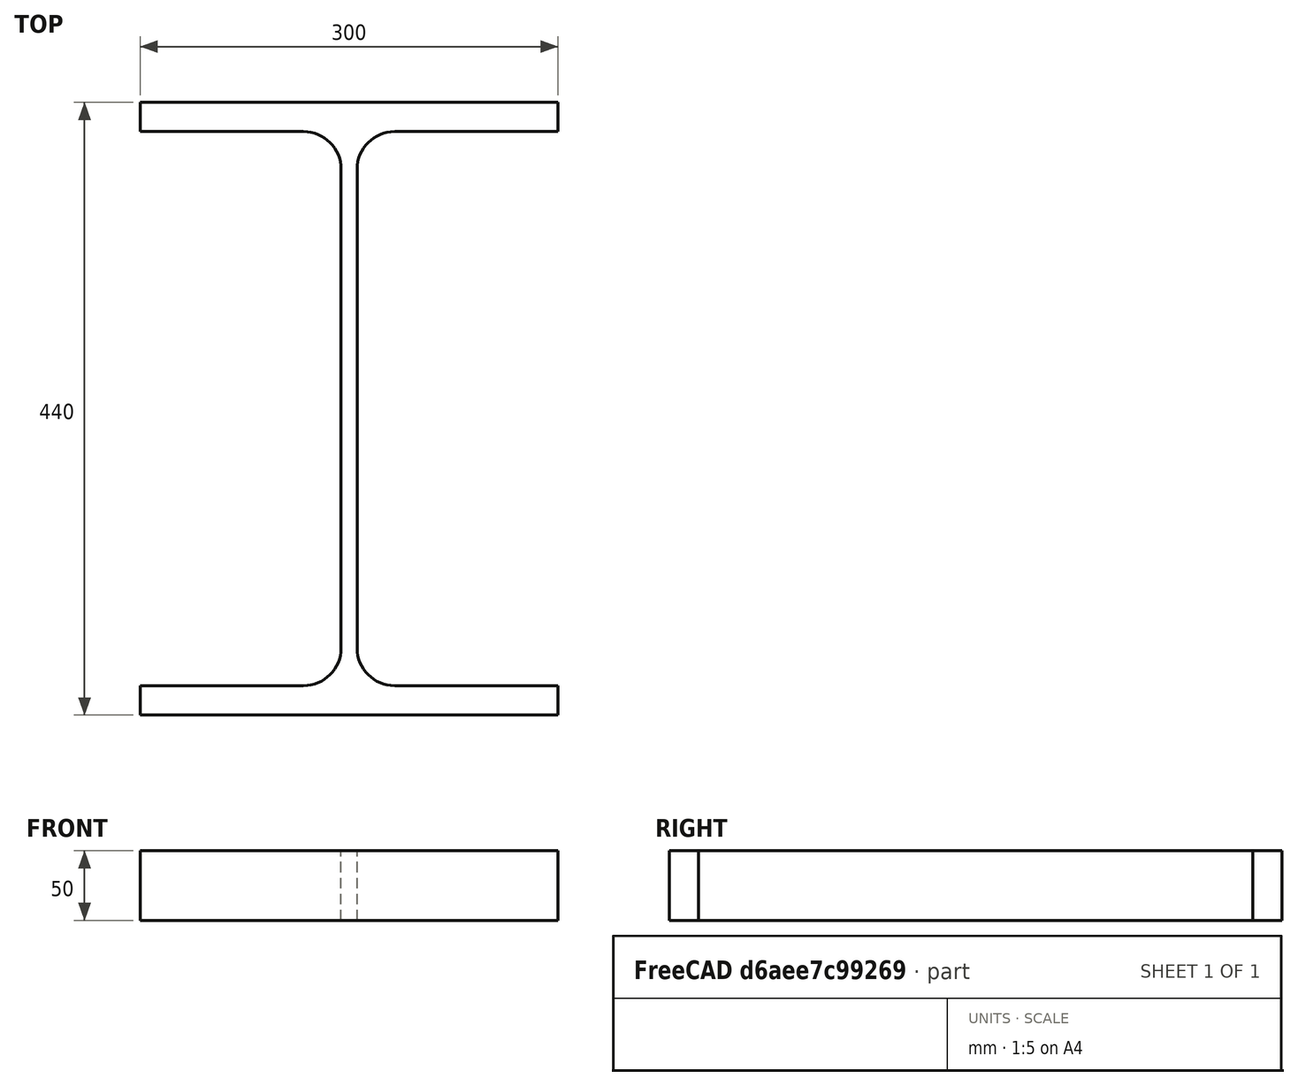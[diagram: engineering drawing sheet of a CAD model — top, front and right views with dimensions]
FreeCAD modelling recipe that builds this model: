
FCSTD DOCUMENT  (FreeCAD 0.15R4671 (Git))
Label: HE-A-Profile 450 DIN1025-3 S235JR
License: All rights reserved
LicenseURL: http://en.wikipedia.org/wiki/All_rights_reserved
objects: Sketcher::SketchObject×1, Part::Extrusion×1
note: 2 computed .brp shape members not serialized (recipe doc carries the construction recipe); baked Part::Feature solids carry a one-line shape summary decoded from their .brp

FEATURE [Sketcher::SketchObject] Sketch
  sketch-geometry (16):
    g0: LineSegment StartX=5.75 StartY=-172 StartZ=0 EndX=5.75 EndY=172 EndZ=0
    g1: LineSegment StartX=32.75 StartY=199 StartZ=0 EndX=150 EndY=199 EndZ=0
    g2: LineSegment StartX=150 StartY=199 StartZ=0 EndX=150 EndY=220 EndZ=0
    g3: LineSegment StartX=150 StartY=220 StartZ=0 EndX=-150 EndY=220 EndZ=0
    g4: LineSegment StartX=-150 StartY=220 StartZ=0 EndX=-150 EndY=199 EndZ=0
    g5: LineSegment StartX=-150 StartY=199 StartZ=0 EndX=-32.75 EndY=199 EndZ=0
    g6: LineSegment StartX=-5.75 StartY=172 StartZ=0 EndX=-5.75 EndY=-172 EndZ=0
    g7: LineSegment StartX=-32.75 StartY=-199 StartZ=0 EndX=-150 EndY=-199 EndZ=0
    g8: LineSegment StartX=-150 StartY=-199 StartZ=0 EndX=-150 EndY=-220 EndZ=0
    g9: LineSegment StartX=-150 StartY=-220 StartZ=0 EndX=150 EndY=-220 EndZ=0
    g10: LineSegment StartX=150 StartY=-220 StartZ=0 EndX=150 EndY=-199 EndZ=0
    g11: LineSegment StartX=150 StartY=-199 StartZ=0 EndX=32.75 EndY=-199 EndZ=0
    g12: ArcOfCircle CenterX=32.75 CenterY=172 CenterZ=0 NormalX=0 NormalY=0 NormalZ=1 Radius=27 StartAngle=1.5708 EndAngle=3.14159
    g13: ArcOfCircle CenterX=32.75 CenterY=-172 CenterZ=0 NormalX=0 NormalY=0 NormalZ=1 Radius=27 StartAngle=3.14159 EndAngle=4.71239
    g14: ArcOfCircle CenterX=-32.75 CenterY=172 CenterZ=0 NormalX=0 NormalY=0 NormalZ=1 Radius=27 StartAngle=0 EndAngle=1.5708
    g15: ArcOfCircle CenterX=-32.75 CenterY=-172 CenterZ=0 NormalX=0 NormalY=0 NormalZ=1 Radius=27 StartAngle=4.71239 EndAngle=6.28319
  constraints (42):
    c: Vertical(g0)
    c: Coincident(g2,g1)
    c: Vertical(g2)
    c: Coincident(g3,g2)
    c: Coincident(g4,g3)
    c: Vertical(g4)
    c: Coincident(g5,g4)
    c: Horizontal(g5)
    c: Vertical(g6)
    c: Horizontal(g7)
    c: Coincident(g8,g7)
    c: Vertical(g8)
    c: Coincident(g9,g8)
    c: Horizontal(g9)
    c: Coincident(g10,g9)
    c: Vertical(g10)
    c: Coincident(g11,g10)
    c: Horizontal(g11)
    c: Tangent(g1,g12) = 1.5708
    c: Tangent(g0,g12) = 1.5708
    c: Tangent(g0,g13) = 1.5708
    c: Tangent(g11,g13) = 1.5708
    c: Tangent(g5,g14) = 1.5708
    c: Tangent(g6,g14) = 1.5708
    c: Tangent(g6,g15) = 1.5708
    c: Tangent(g7,g15) = 1.5708
    c: Equal(g3,g9)
    c: Equal(g2,g4)
    c: Equal(g4,g8)
    c: Equal(g8,g10)
    c: Equal(g12,g14)
    c: Equal(g14,g15)
    c: Equal(g15,g13)
    c: Symmetric(g2,g3,g-2)
    c: Symmetric(g9,g8,g-2)
    c: Symmetric(g0,g6,g-2)
    c: Symmetric(g2,g9,g-1)
    c: DistanceY(g2,g9) = -440
    c: DistanceX(g3) = -300
    c: DistanceX(g0,g6) = -11.5
    c: DistanceY(g2) = 21
    c: Radius(g12) = 27
FEATURE [Part::Extrusion] Extrude  label="HE-A-Profile 450 DIN1025-3 S235JR"
  Base = -> Sketch
  Dir = (0,0,50)
  Solid = true
